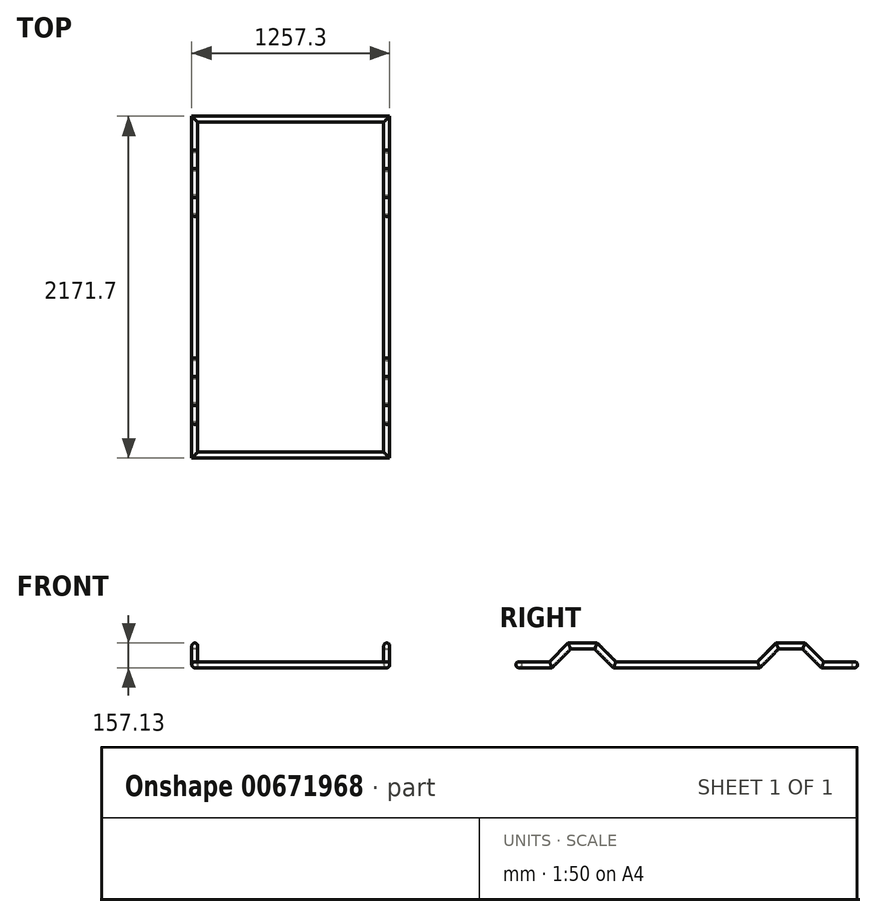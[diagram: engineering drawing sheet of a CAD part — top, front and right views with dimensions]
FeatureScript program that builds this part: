
annotation { "Feature Type Name" : "Feature", "Feature Type Description" : "" }
export const myFeature = defineFeature(function(context is Context, id is Id, definition is map)
    precondition{}
    {
        {
            var Q0;
            Q0=qCreatedBy(makeId("Top.planeOp"),FACE);
            var sketch = newSketch(context, id + "F0", { "sketchPlane" : qUnion([Q0])});
            skLineSegment(sketch, "E0", {"start": v(-609.6, 0) * mm, "end": v(609.6, 0) * mm});
            skLineSegment(sketch, "E1", {"start": v(609.6, 0) * mm, "end": v(609.6, 203.2) * mm});
            skLineSegment(sketch, "E2", {"start": v(609.6, 2133.6) * mm, "end": v(-609.6, 2133.6) * mm});
            skLineSegment(sketch, "E3", {"start": v(-609.6, 2133.6) * mm, "end": v(-609.6, 1930.4) * mm});
            skPoint(sketch, "E4", {"position": v(0, 0) * mm});
            skPoint(sketch, "E5", {"position": v(-609.6, 203.2) * mm});
            skPoint(sketch, "E6", {"position": v(609.6, 203.2) * mm});
            skPoint(sketch, "E7", {"position": v(-609.6, 609.6) * mm});
            skPoint(sketch, "E8", {"position": v(609.6, 609.6) * mm});
            skPoint(sketch, "E9", {"position": v(-609.6, 1930.4) * mm});
            skPoint(sketch, "E10", {"position": v(-609.6, 1524) * mm});
            skPoint(sketch, "E11", {"position": v(609.6, 1524) * mm});
            skPoint(sketch, "E12", {"position": v(609.6, 1930.4) * mm});
            skLineSegment(sketch, "E13", {"start": v(-609.6, 203.2) * mm, "end": v(-609.6, 0) * mm});
            skLineSegment(sketch, "E14", {"start": v(-609.6, 609.6) * mm, "end": v(-609.6, 203.2) * mm});
            skLineSegment(sketch, "E15", {"start": v(-609.6, 1524) * mm, "end": v(-609.6, 609.6) * mm});
            skLineSegment(sketch, "E16", {"start": v(-609.6, 1930.4) * mm, "end": v(-609.6, 1524) * mm});
            skLineSegment(sketch, "E17", {"start": v(609.6, 1930.4) * mm, "end": v(609.6, 2133.6) * mm});
            skLineSegment(sketch, "E18", {"start": v(609.6, 1524) * mm, "end": v(609.6, 1930.4) * mm});
            skLineSegment(sketch, "E19", {"start": v(609.6, 609.6) * mm, "end": v(609.6, 1524) * mm});
            skLineSegment(sketch, "E20", {"start": v(609.6, 203.2) * mm, "end": v(609.6, 609.6) * mm});
            skSolve(sketch);
        }
        {
            var Q0;
            Q0=qCreatedBy(makeId("Front.planeOp"),FACE);
            var Q1;
            Q1=sQuery(id+"F0.wireOp",VERTEX,"E13.end");
            cPlane(context, id + "F1", {"entities" : qUnion([Q0, Q1]), "cplaneType" : CPlaneType.PLANE_POINT, "offset" : 25.4 * mm, "width" : 152.4 * mm, "height" : 152.4 * mm});
        }
        {
            var Q0;
            Q0=qCreatedBy(id+"F1.planeOp",FACE);
            var sketch = newSketch(context, id + "F2", { "sketchPlane" : qUnion([Q0])});
            skPoint(sketch, "E21", {"position": v(-609.6, 0) * mm});
            skCircle(sketch, "E22", {"center": v(-609.6, 0) * mm, "radius": 19.05 * mm});
            skSolve(sketch);
        }
        {
            var Q0;
            Q0=qCreatedBy(makeId("Right.planeOp"),FACE);
            var Q1;
            Q1=sQuery(id+"F2.wireOp",VERTEX,"E21");
            cPlane(context, id + "F3", {"entities" : qUnion([Q0, Q1]), "cplaneType" : CPlaneType.PLANE_POINT, "offset" : 25.4 * mm, "width" : 152.4 * mm, "height" : 152.4 * mm});
        }
        {
            var Q0;
            Q0=qCreatedBy(id+"F3.planeOp",FACE);
            var sketch = newSketch(context, id + "F4", { "sketchPlane" : qUnion([Q0])});
            skLineSegment(sketch, "E23.0", {"start": v(2133.6, 0) * mm, "end": v(1930.4, 0) * mm});
            skPoint(sketch, "E24", {"position": v(203.2, 0) * mm});
            skPoint(sketch, "E25", {"position": v(609.6, 0) * mm});
            skLineSegment(sketch, "E26", {"start": v(609.6, 0) * mm, "end": v(490.57, 119.03) * mm});
            skLineSegment(sketch, "E27", {"start": v(490.57, 119.03) * mm, "end": v(322.23, 119.03) * mm});
            skLineSegment(sketch, "E28", {"start": v(322.23, 119.03) * mm, "end": v(203.2, 0) * mm});
            skPoint(sketch, "E29", {"position": v(1524, 0) * mm});
            skPoint(sketch, "E30", {"position": v(1930.4, 0) * mm});
            skLineSegment(sketch, "E31", {"start": v(1524, 0) * mm, "end": v(1643.03, 119.03) * mm});
            skLineSegment(sketch, "E32", {"start": v(1643.03, 119.03) * mm, "end": v(1811.37, 119.03) * mm});
            skLineSegment(sketch, "E33", {"start": v(1811.37, 119.03) * mm, "end": v(1930.4, 0) * mm});
            skSolve(sketch);
        }
        {
            var Q0;
            Q0=qCreatedBy(makeId("Right.planeOp"),FACE);
            var Q1;
            Q1=sQuery(id+"F0.wireOp",VERTEX,"E1.start");
            cPlane(context, id + "F5", {"entities" : qUnion([Q0, Q1]), "cplaneType" : CPlaneType.PLANE_POINT, "offset" : 25.4 * mm, "width" : 152.4 * mm, "height" : 152.4 * mm});
        }
        {
            var Q0;
            Q0=qCreatedBy(id+"F5.planeOp",FACE);
            var sketch = newSketch(context, id + "F6", { "sketchPlane" : qUnion([Q0])});
            skPoint(sketch, "E34", {"position": v(203.2, 0) * mm});
            skPoint(sketch, "E35", {"position": v(609.6, 0) * mm});
            skPoint(sketch, "E36", {"position": v(1524, 0) * mm});
            skPoint(sketch, "E37", {"position": v(1930.4, 0) * mm});
            skLineSegment(sketch, "E38", {"start": v(203.2, 0) * mm, "end": v(322.23, 119.03) * mm});
            skLineSegment(sketch, "E39", {"start": v(490.57, 119.03) * mm, "end": v(609.6, 0) * mm});
            skLineSegment(sketch, "E40", {"start": v(490.57, 119.03) * mm, "end": v(322.23, 119.03) * mm});
            skLineSegment(sketch, "E41", {"start": v(1524, 0) * mm, "end": v(1643.03, 119.03) * mm});
            skLineSegment(sketch, "E42", {"start": v(1643.03, 119.03) * mm, "end": v(1811.37, 119.03) * mm});
            skLineSegment(sketch, "E43", {"start": v(1811.37, 119.03) * mm, "end": v(1930.4, 0) * mm});
            skSolve(sketch);
        }
        {
            var Q0;
            Q0=makeQuery(id+"F2.imprint","IMPRINT",FACE,{"disambiguationData":[TD([[makeQuery(id+"F2.imprint","IMPRINT",EDGE,{"derivedFrom":sQuery(id+"F2.wireOp",EDGE,"E22")}),1.0]])]});
            var Q1;
            Q1=sQuery(id+"F0.wireOp",EDGE,"E13");
            var Q2;
            Q2=sQuery(id+"F4.wireOp",EDGE,"E28");
            var Q3;
            Q3=sQuery(id+"F4.wireOp",EDGE,"E27");
            var Q4;
            Q4=sQuery(id+"F4.wireOp",EDGE,"E26");
            var Q5;
            Q5=sQuery(id+"F0.wireOp",EDGE,"E15");
            var Q6;
            Q6=sQuery(id+"F4.wireOp",EDGE,"E31");
            var Q7;
            Q7=sQuery(id+"F4.wireOp",EDGE,"E32");
            var Q8;
            Q8=sQuery(id+"F4.wireOp",EDGE,"E33");
            var Q9;
            Q9=sQuery(id+"F4.wireOp",EDGE,"E23.0");
            var Q10;
            Q10=sQuery(id+"F0.wireOp",EDGE,"E2");
            var Q11;
            Q11=sQuery(id+"F0.wireOp",EDGE,"E17");
            var Q12;
            Q12=sQuery(id+"F6.wireOp",EDGE,"E43");
            var Q13;
            Q13=sQuery(id+"F6.wireOp",EDGE,"E42");
            var Q14;
            Q14=sQuery(id+"F6.wireOp",EDGE,"E41");
            var Q15;
            Q15=sQuery(id+"F0.wireOp",EDGE,"E19");
            var Q16;
            Q16=sQuery(id+"F6.wireOp",EDGE,"E39");
            var Q17;
            Q17=sQuery(id+"F6.wireOp",EDGE,"E40");
            var Q18;
            Q18=sQuery(id+"F6.wireOp",EDGE,"E38");
            var Q19;
            Q19=sQuery(id+"F0.wireOp",EDGE,"E1");
            var Q20;
            Q20=sQuery(id+"F0.wireOp",EDGE,"E0");
            sweep(context, id + "F7", {"profiles" : qUnion([Q0]), "path" : qUnion([Q1, Q2, Q3, Q4, Q5, Q6, Q7, Q8, Q9, Q10, Q11, Q12, Q13, Q14, Q15, Q16, Q17, Q18, Q19, Q20])});
        }
    });
